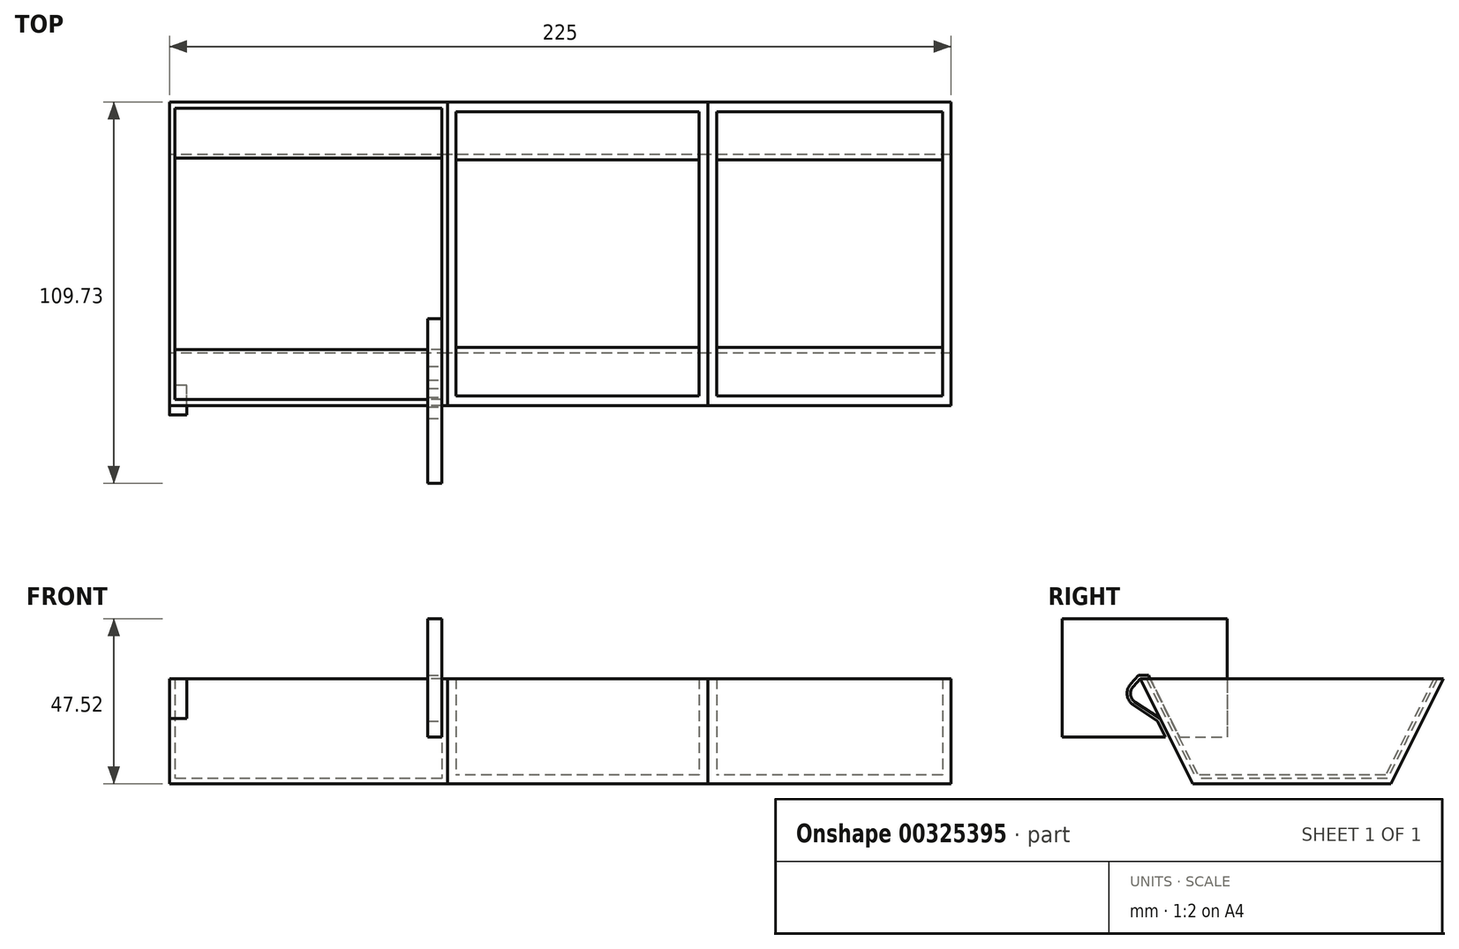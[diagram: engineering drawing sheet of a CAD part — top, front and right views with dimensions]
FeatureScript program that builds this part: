
annotation { "Feature Type Name" : "Feature", "Feature Type Description" : "" }
export const myFeature = defineFeature(function(context is Context, id is Id, definition is map)
    precondition{}
    {
        {
            var Q0;
            Q0=qCreatedBy(makeId("Right.planeOp"),FACE);
            var sketch = newSketch(context, id + "F0", { "sketchPlane" : qUnion([Q0])});
            skLineSegment(sketch, "E0", {"start": v(0, 0) * mm, "end": v(0, 30.27) * mm});
            skLineSegment(sketch, "E1", {"start": v(0, 30.27) * mm, "end": v(43.67, 30.27) * mm});
            skLineSegment(sketch, "E2", {"start": v(43.67, 30.27) * mm, "end": v(28.55, 0) * mm});
            skLineSegment(sketch, "E3", {"start": v(28.55, 0) * mm, "end": v(0, 0) * mm});
            skSolve(sketch);
        }
        {
            var Q0;
            Q0=makeQuery(id+"F0.imprint","IMPRINT",FACE,{"disambiguationData":[TD([[makeQuery(id+"F0.imprint","IMPRINT",EDGE,{"derivedFrom":sQuery(id+"F0.wireOp",EDGE,"E0")}),-1.0]])]});
            extrude(context, id + "F1", {"entities" : qUnion([Q0]), "depth" : 80 * mm});
        }
        {
            var Q0;
            Q0=makeQuery(id+"F1.opExtrude","SWEPT_BODY",BODY,{"disambiguationData":[OSD([sQuery(id+"F0.wireOp",EDGE,"E0"),sQuery(id+"F0.wireOp",EDGE,"E1"),sQuery(id+"F0.wireOp",EDGE,"E2"),sQuery(id+"F0.wireOp",EDGE,"E3")])]});
            var Q1;
            Q1=makeQuery(id+"F1.opExtrude","SWEPT_FACE",FACE,{"disambiguationData":[OSD([sQuery(id+"F0.wireOp",EDGE,"E0")])]});
            mirror(context, id + "F2", {"operationType" : NewBodyOperationType.ADD, "entities" : qUnion([Q0]), "mirrorPlane" : qUnion([Q1])});
        }
        {
            var Q0;
            {var subQ0=makeQuery(id+"F1.opExtrude","SWEPT_FACE",FACE,{"disambiguationData":[OSD([sQuery(id+"F0.wireOp",EDGE,"E1")])]});Q0=makeQuery(id+"F2.boolean.opBoolean","MERGE",FACE,{"derivedFrom":[subQ0,makeQuery(id+"F2.opPattern","COPY",FACE,{"derivedFrom":subQ0,"instanceName":"1"})]});}
            shell(context, id + "F3", {"entities" : qUnion([Q0]), "thickness" : 1.6 * mm});
        }
        {
            var Q0;
            {var subQ0=makeQuery(id+"F1.opExtrude","CAP_FACE",FACE,{"disambiguationData":[OSD([sQuery(id+"F0.wireOp",EDGE,"E0"),sQuery(id+"F0.wireOp",EDGE,"E1"),sQuery(id+"F0.wireOp",EDGE,"E2"),sQuery(id+"F0.wireOp",EDGE,"E3")])],"isStart":false});Q0=makeQuery(id+"F2.boolean.opBoolean","MERGE",FACE,{"derivedFrom":[subQ0,makeQuery(id+"F2.opPattern","COPY",FACE,{"derivedFrom":subQ0,"instanceName":"1"})]});}
            extrude(context, id + "F4", {"entities" : qUnion([Q0]), "depth" : 75 * mm});
        }
        {
            var Q0;
            Q0=makeQuery(id+"F4.opExtrude","CAP_FACE",FACE,{"disambiguationData":[OSD([sQuery(id+"F0.wireOp",EDGE,"E0"),sQuery(id+"F0.wireOp",EDGE,"E1"),sQuery(id+"F0.wireOp",EDGE,"E2"),sQuery(id+"F0.wireOp",EDGE,"E3")])],"isStart":false});
            extrude(context, id + "F5", {"entities" : qUnion([Q0]), "depth" : 70 * mm});
        }
        {
            var Q0;
            Q0=makeQuery(id+"F4.opExtrude","SWEPT_FACE",FACE,{"disambiguationData":[OSD([sQuery(id+"F0.wireOp",EDGE,"E1")])]});
            shell(context, id + "F6", {"entities" : qUnion([Q0]), "thickness" : 2.5 * mm});
        }
        {
            var Q0;
            Q0=makeQuery(id+"F5.opExtrude","SWEPT_FACE",FACE,{"disambiguationData":[OSD([sQuery(id+"F0.wireOp",EDGE,"E1")])]});
            shell(context, id + "F7", {"entities" : qUnion([Q0]), "thickness" : 2.5 * mm});
        }
        {
            var Q0;
            {var subQ0=makeQuery(id+"F1.opExtrude","CAP_FACE",FACE,{"disambiguationData":[OSD([sQuery(id+"F0.wireOp",EDGE,"E0"),sQuery(id+"F0.wireOp",EDGE,"E1"),sQuery(id+"F0.wireOp",EDGE,"E2"),sQuery(id+"F0.wireOp",EDGE,"E3")])],"isStart":true});Q0=makeQuery(id+"F2.boolean.opBoolean","MERGE",FACE,{"derivedFrom":[subQ0,makeQuery(id+"F2.opPattern","COPY",FACE,{"derivedFrom":subQ0,"instanceName":"1"})]});}
            var sketch = newSketch(context, id + "F8", { "sketchPlane" : qUnion([Q0])});
            skLineSegment(sketch, "E4", {"start": v(43.67, 30.27) * mm, "end": v(47.94, 25.44) * mm});
            skLineSegment(sketch, "E5", {"start": v(47.94, 25.44) * mm, "end": v(37.93, 18.77) * mm});
            skLineSegment(sketch, "E6", {"start": v(37.93, 18.77) * mm, "end": v(43.67, 30.27) * mm});
            skSolve(sketch);
        }
        {
            var Q0;
            Q0=makeQuery(id+"F8.imprint","IMPRINT",FACE,{"disambiguationData":[TD([[makeQuery(id+"F8.imprint","IMPRINT",EDGE,{"derivedFrom":sQuery(id+"F8.wireOp",EDGE,"E4")}),-1.0]])]});
            extrude(context, id + "F9", {"entities" : qUnion([Q0]), "operationType" : NewBodyOperationType.ADD, "oppositeDirection" : true, "depth" : 5 * mm});
        }
        {
            var Q0;
            Q0=makeQuery(id+"F9.opExtrude","SWEPT_EDGE",EDGE,{"disambiguationData":[OSD([sQuery(id+"F8.wireOp",EDGE,"E4"),sQuery(id+"F8.wireOp",EDGE,"E5")])]});
            fillet(context, id + "F10", {"entities" : qUnion([Q0]), "radius" : 3 * mm, "tangentPropagation" : true, "allowEdgeOverflow" : false});
        }
        {
            var Q0;
            {var subQ0=sQuery(id+"F0.wireOp",EDGE,"E3");var subQ1=sQuery(id+"F0.wireOp",EDGE,"E2");var subQ2=sQuery(id+"F0.wireOp",EDGE,"E1");var subQ3=sQuery(id+"F0.wireOp",EDGE,"E0");var subQ4=makeQuery(id+"F1.opExtrude","CAP_FACE",FACE,{"disambiguationData":[OSD([subQ3,subQ2,subQ1,subQ0])],"isStart":false});Q0=makeQuery(id+"F3.opShell","OFFSET_FACE",FACE,{"disambiguationData":[OSD([subQ3,subQ2,subQ1,subQ0]),TDD([makeQuery(id+"F2.boolean.opBoolean","MERGE",FACE,{"derivedFrom":[subQ4,makeQuery(id+"F2.opPattern","COPY",FACE,{"derivedFrom":subQ4,"instanceName":"1"})]})])]});}
            var sketch = newSketch(context, id + "F11", { "sketchPlane" : qUnion([Q0])});
            skLineSegment(sketch, "E7.0", {"start": v(43.67, 30.27) * mm, "end": v(45.66, 28.02) * mm});
            skArc(sketch, "E8.0", {"start": v(45.66, 28.02) * mm, "mid": v(46.4, 25.64) * mm, "end": v(45.08, 23.53) * mm});
            skLineSegment(sketch, "E9.0", {"start": v(45.08, 23.53) * mm, "end": v(37.93, 18.77) * mm});
            skLineSegment(sketch, "E10.0", {"start": v(37.93, 18.77) * mm, "end": v(28.55, 0) * mm});
            skLineSegment(sketch, "E11.0", {"start": v(41.88, 30.27) * mm, "end": v(27.57, 1.6) * mm});
            skLineSegment(sketch, "E12", {"start": v(43.67, 30.27) * mm, "end": v(41.88, 30.27) * mm});
            skLineSegment(sketch, "E13.bottom", {"start": v(66.06, 47.52) * mm, "end": v(18.64, 47.52) * mm});
            skLineSegment(sketch, "E13.top", {"start": v(66.06, 13.44) * mm, "end": v(36.38, 13.44) * mm});
            skLineSegment(sketch, "E13.left", {"start": v(66.06, 47.52) * mm, "end": v(66.06, 13.44) * mm});
            skLineSegment(sketch, "E13.right", {"start": v(18.64, 47.52) * mm, "end": v(18.64, 13.44) * mm});
            skLineSegment(sketch, "E14.0", {"start": v(38.7, 18.09) * mm, "end": v(36.38, 13.44) * mm});
            skLineSegment(sketch, "E14.1", {"start": v(45.63, 22.7) * mm, "end": v(38.7, 18.09) * mm});
            skLineSegment(sketch, "E14.2", {"start": v(41.26, 31.27) * mm, "end": v(32.36, 13.44) * mm});
            skLineSegment(sketch, "E14.3", {"start": v(44.12, 31.27) * mm, "end": v(41.26, 31.27) * mm});
            skLineSegment(sketch, "E14.4", {"start": v(44.12, 31.27) * mm, "end": v(46.41, 28.68) * mm});
            skArc(sketch, "E14.5", {"start": v(46.41, 28.68) * mm, "mid": v(47.38, 25.51) * mm, "end": v(45.63, 22.7) * mm});
            skLineSegment(sketch, "E15.trimOffspring", {"start": v(32.36, 13.44) * mm, "end": v(18.64, 13.44) * mm});
            skLineSegment(sketch, "E16.trimOffspring", {"start": v(35.26, 13.44) * mm, "end": v(33.48, 13.44) * mm});
            skSolve(sketch);
        }
        {
            var Q0;
            {var subQ6=sQuery(id+"F11.wireOp",EDGE,"E13.bottom");Q0=makeQuery(id+"F11.imprint","IMPRINT",FACE,{"disambiguationData":[TD([[makeQuery(id+"F11.imprint","IMPRINT",EDGE,{"derivedFrom":subQ6}),1.0]])]});}
            var Q1;
            {var subQ0=sQuery(id+"F11.wireOp",EDGE,"E15.trimOffspring");Q1=makeQuery(id+"F11.imprint","IMPRINT",FACE,{"disambiguationData":[TD([[makeQuery(id+"F11.imprint","IMPRINT",EDGE,{"derivedFrom":subQ0}),-1.0]])]});}
            extrude(context, id + "F12", {"entities" : qUnion([Q0, Q1]), "depth" : 4 * mm});
        }
    });
